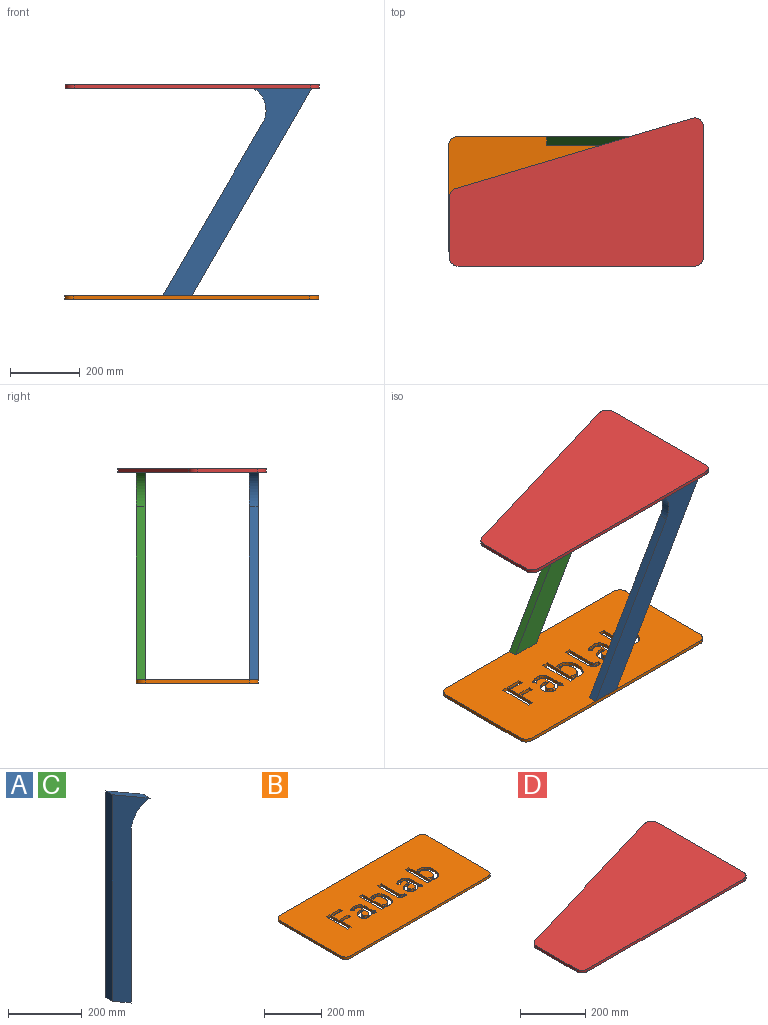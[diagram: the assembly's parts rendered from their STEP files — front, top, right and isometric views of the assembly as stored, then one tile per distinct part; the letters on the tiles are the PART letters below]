
ASSEMBLY  parts=4 mates=3
PART A: 7 faces, bbox 144x25x726 mm
  f0: plane 684.43x25mm, normal (-1,0,0), area 17110.8mm2, adj f3,f4,f5,f6
  f1: plane 570.86x25mm, normal (1,0,0), area 14271.5mm2, adj f2,f4,f5,f6
  f2: cylinder r=72mm len=72mm, axis (0,1,0), area 2827.4mm2, adj f1,f3,f4,f5
  f3: plane 144x83.14mm, normal (0.5,0,0.87), area 4156.9mm2, adj f0,f2,f4,f5
  f4: plane 726x144mm, normal (0,-1,0), area 51888mm2, adj f0,f1,f2,f3,f6
  f5: plane 726x144mm, normal (0,1,0), area 51888mm2, adj f0,f1,f2,f3,f6
  f6: plane 72x41.57mm, normal (-0.5,0,-0.87), area 2078.5mm2, adj f0,f1,f4,f5
PART B: 213 faces, bbox 726x348.5x10 mm
  f0: plane 298.48x10mm, normal (-1,0,0), area 2984.8mm2, adj f4,f5,f6,f9
  f1: plane 676x10mm, normal (0,-1,0), area 6760mm2, adj f4,f5,f6,f7
  f2: plane 298.48x10mm, normal (1,0,0), area 2984.8mm2, adj f4,f5,f7,f8
  f3: plane 676x10mm, normal (0,1,0), area 6760mm2, adj f4,f5,f8,f9
  f4: plane 726x348.48mm, normal (0,0,1), area 234382.8mm2, adj f0,f1,f2,f3,f6,f7,f8,f9
  f5: plane 726x348.48mm, normal (0,0,-1), area 234382.8mm2, adj f0,f1,f2,f3,f6,f7,f8,f9
  f6: cylinder r=25mm len=25mm, axis (0,0,1), area 392.7mm2, adj f0,f1,f4,f5
  f7: cylinder r=25mm len=25mm, axis (0,0,-1), area 392.7mm2, adj f1,f2,f4,f5
  f8: cylinder r=25mm len=25mm, axis (0,0,1), area 392.7mm2, adj f2,f3,f4,f5
  f9: cylinder r=25mm len=25mm, axis (0,0,-1), area 392.7mm2, adj f0,f3,f4,f5
  f10: plane 104.61x10mm, normal (1,0,0), area 1046.1mm2, adj f4,f5,f11,f212
  f11: plane 17.31x10mm, normal (0,-1,0), area 173.1mm2, adj f4,f5,f10,f12
  f12: plane 104.61x10mm, normal (-1,0,0), area 1046.1mm2, adj f4,f5,f11,f212
  f13: plane 11.65x10mm, normal (-1,0,0), area 116.5mm2, adj f4,f5,f14,f201
  f14: plane 37.88x10mm, normal (0,1,0), area 378.8mm2, adj f4,f5,f13,f15
  f15: plane 11.65x10mm, normal (1,0,0), area 116.5mm2, adj f4,f5,f14,f201
  f16: plane 42.29x10mm, normal (0,-1,0), area 422.9mm2, adj f4,f5,f17,f202
  f17: plane 12.9x10mm, normal (-1,0,0), area 129mm2, adj f4,f5,f16,f18
  f18: plane 42.29x10mm, normal (0,1,0), area 422.9mm2, adj f4,f5,f17,f202
  f19: extruded ~10x7.45mm, area 77.5mm2, adj f4,f5,f20,f203
  f20: extruded ~10x9.53mm, area 100.8mm2, adj f4,f5,f19,f21
  f21: extruded ~10x7.6mm, area 86.6mm2, adj f4,f5,f20,f22
  f22: plane 11.49x10mm, normal (-1,0,0), area 114.9mm2, adj f4,f5,f21,f23
  f23: extruded ~10x1.84mm, area 18.5mm2, adj f4,f5,f22,f24
  f24: extruded ~10x9.3mm, area 94.2mm2, adj f4,f5,f23,f25
  f25: extruded ~10x7.87mm, area 89.4mm2, adj f4,f5,f24,f26
  f26: extruded ~10x7.53mm, area 93.2mm2, adj f4,f5,f25,f27
  f27: extruded ~11.5x10mm, area 117.4mm2, adj f4,f5,f26,f28
  f28: extruded ~11.28x10mm, area 117.5mm2, adj f4,f5,f27,f29
  f29: extruded ~10x7.81mm, area 106.4mm2, adj f4,f5,f28,f30
  f30: extruded ~10x9.86mm, area 109.1mm2, adj f4,f5,f29,f31
  f31: extruded ~11.21x10mm, area 113.4mm2, adj f4,f5,f30,f32
  f32: plane 10x6.25mm, normal (0,-1,0), area 62.5mm2, adj f4,f5,f31,f33
  f33: plane 10.08x10mm, normal (-1,0,0), area 100.8mm2, adj f4,f5,f32,f34
  f34: plane 10x3.11mm, normal (0,1,0), area 31.1mm2, adj f4,f5,f33,f35
  f35: extruded ~10x5.96mm, area 60mm2, adj f4,f5,f34,f36
  f36: extruded ~10x5.83mm, area 62.3mm2, adj f4,f5,f35,f203
  f37: plane 19.58x10mm, normal (-1,0,0), area 195.8mm2, adj f4,f5,f38,f204
  f38: extruded ~10x3.34mm, area 33.4mm2, adj f4,f5,f37,f39
  f39: extruded ~10x4.47mm, area 45.1mm2, adj f4,f5,f38,f40
  f40: extruded ~10x4.11mm, area 43.4mm2, adj f4,f5,f39,f41
  f41: extruded ~10x2.49mm, area 35.5mm2, adj f4,f5,f40,f42
  f42: plane 10x9.52mm, normal (-0.9,0.43,0), area 105.4mm2, adj f4,f5,f41,f43
  f43: extruded ~10x3.91mm, area 40.2mm2, adj f4,f5,f42,f44
  f44: extruded ~10x3.97mm, area 46.6mm2, adj f4,f5,f43,f45
  f45: extruded ~10x3.48mm, area 47.8mm2, adj f4,f5,f44,f46
  f46: extruded ~10x4.19mm, area 46.9mm2, adj f4,f5,f45,f47
  f47: extruded ~10x6.31mm, area 85.8mm2, adj f4,f5,f46,f48
  f48: extruded ~10x9.3mm, area 101.9mm2, adj f4,f5,f47,f49
  f49: plane 10.79x10mm, normal (1,0,0), area 107.9mm2, adj f4,f5,f48,f50
  f50: extruded ~10x6.18mm, area 68.2mm2, adj f4,f5,f49,f51
  f51: extruded ~10x4.89mm, area 68.6mm2, adj f4,f5,f50,f52
  f52: plane 29.96x10mm, normal (1,0,0), area 299.6mm2, adj f4,f5,f51,f53
  f53: extruded ~11.07x10mm, area 111.1mm2, adj f4,f5,f52,f54
  f54: extruded ~10x6.04mm, area 65.9mm2, adj f4,f5,f53,f55
  f55: extruded ~10x4.19mm, area 49.2mm2, adj f4,f5,f54,f56
  f56: extruded ~10x5.89mm, area 59.2mm2, adj f4,f5,f55,f57
  f57: extruded ~10x5.88mm, area 59.5mm2, adj f4,f5,f56,f58
  f58: extruded ~10x5.11mm, area 54.4mm2, adj f4,f5,f57,f59
  f59: extruded ~10x4.11mm, area 47.4mm2, adj f4,f5,f58,f60
  f60: extruded ~10x2.63mm, area 33mm2, adj f4,f5,f59,f61
  f61: plane 10x9.79mm, normal (0.84,0.55,0), area 116.9mm2, adj f4,f5,f60,f62
  f62: extruded ~10x4.25mm, area 53.4mm2, adj f4,f5,f61,f63
  f63: extruded ~10x6.53mm, area 71.6mm2, adj f4,f5,f62,f64
  f64: extruded ~10x8.03mm, area 83mm2, adj f4,f5,f63,f65
  f65: extruded ~10x9.02mm, area 90.6mm2, adj f4,f5,f64,f66
  f66: extruded ~10x8.3mm, area 83.6mm2, adj f4,f5,f65,f67
  f67: extruded ~10x7.38mm, area 79.5mm2, adj f4,f5,f66,f68
  f68: extruded ~10x5.81mm, area 79.4mm2, adj f4,f5,f67,f69
  f69: extruded ~10x8.29mm, area 90.7mm2, adj f4,f5,f68,f70
  f70: extruded ~10.02x10mm, area 101.1mm2, adj f4,f5,f69,f204
  f71: plane 110.29x10mm, normal (1,0,0), area 1102.9mm2, adj f4,f5,f72,f205
  f72: plane 17.17x10mm, normal (0,-1,0), area 171.7mm2, adj f4,f5,f71,f73
  f73: plane 100.77x10mm, normal (-1,0,0), area 1007.7mm2, adj f4,f5,f72,f74
  f74: extruded ~10x4.55mm, area 45.7mm2, adj f4,f5,f73,f75
  f75: extruded ~10x4.96mm, area 49.8mm2, adj f4,f5,f74,f205
  f76: extruded ~11.64x10mm, area 128.7mm2, adj f4,f5,f77,f206
  f77: extruded ~14.33x10mm, area 144.7mm2, adj f4,f5,f76,f78
  f78: extruded ~15.75x10mm, area 159.1mm2, adj f4,f5,f77,f79
  f79: extruded ~13.56x10mm, area 148.3mm2, adj f4,f5,f78,f80
  f80: extruded ~10x9.79mm, area 136.7mm2, adj f4,f5,f79,f81
  f81: extruded ~13.83x10mm, area 144.4mm2, adj f4,f5,f80,f82
  f82: extruded ~10x9.52mm, area 96.1mm2, adj f4,f5,f81,f83
  f83: extruded ~10x7.81mm, area 84.4mm2, adj f4,f5,f82,f84
  f84: plane 14.76x10mm, normal (1,0,0), area 147.6mm2, adj f4,f5,f83,f85
  f85: extruded ~10x5.04mm, area 64.5mm2, adj f4,f5,f84,f86
  f86: extruded ~10x6.45mm, area 67mm2, adj f4,f5,f85,f87
  f87: extruded ~10x7.74mm, area 81.4mm2, adj f4,f5,f86,f88
  f88: extruded ~10x5.96mm, area 83.4mm2, adj f4,f5,f87,f89
  f89: extruded ~10x8.59mm, area 95mm2, adj f4,f5,f88,f90
  f90: extruded ~10.64x10mm, area 107.8mm2, adj f4,f5,f89,f91
  f91: extruded ~10.52x10mm, area 106.3mm2, adj f4,f5,f90,f92
  f92: extruded ~10x8.8mm, area 95.8mm2, adj f4,f5,f91,f93
  f93: extruded ~10x6.1mm, area 84.5mm2, adj f4,f5,f92,f94
  f94: extruded ~10x7.65mm, area 81mm2, adj f4,f5,f93,f95
  f95: extruded ~10x6.76mm, area 69.8mm2, adj f4,f5,f94,f96
  f96: extruded ~10x5.46mm, area 70.2mm2, adj f4,f5,f95,f97
  f97: plane 15.19x10mm, normal (1,0,0), area 151.9mm2, adj f4,f5,f96,f98
  f98: extruded ~10x7.25mm, area 78mm2, adj f4,f5,f97,f99
  f99: extruded ~10x8.22mm, area 83mm2, adj f4,f5,f98,f100
  f100: extruded ~10x9.53mm, area 96.4mm2, adj f4,f5,f99,f101
  f101: extruded ~10x9.01mm, area 100.2mm2, adj f4,f5,f100,f206
  f102: plane 85.87x10mm, normal (-1,0,0), area 858.7mm2, adj f4,f5,f103,f207
  f103: extruded ~10x7.59mm, area 77.5mm2, adj f4,f5,f102,f104
  f104: extruded ~10x4.12mm, area 55.2mm2, adj f4,f5,f103,f105
  f105: extruded ~10x5.18mm, area 55.1mm2, adj f4,f5,f104,f106
  f106: extruded ~10x6.31mm, area 63.3mm2, adj f4,f5,f105,f107
  f107: plane 10.52x10mm, normal (-1,0,0), area 105.2mm2, adj f4,f5,f106,f108
  f108: extruded ~10x3.82mm, area 38.4mm2, adj f4,f5,f107,f109
  f109: extruded ~10x3.7mm, area 37.1mm2, adj f4,f5,f108,f110
  f110: extruded ~10x4.25mm, area 42.5mm2, adj f4,f5,f109,f111
  f111: extruded ~10x4.27mm, area 42.7mm2, adj f4,f5,f110,f112
  f112: extruded ~10x3.84mm, area 38.6mm2, adj f4,f5,f111,f113
  f113: extruded ~10x7.52mm, area 88.1mm2, adj f4,f5,f112,f114
  f114: extruded ~10x7.3mm, area 84.3mm2, adj f4,f5,f113,f115
  f115: extruded ~10x7.88mm, area 81mm2, adj f4,f5,f114,f116
  f116: extruded ~10x5.97mm, area 59.9mm2, adj f4,f5,f115,f117
  f117: plane 85.01x10mm, normal (1,0,0), area 850.1mm2, adj f4,f5,f116,f207
  f118: extruded ~10x7.45mm, area 77.5mm2, adj f4,f5,f119,f208
  f119: extruded ~10x9.53mm, area 100.8mm2, adj f4,f5,f118,f120
  f120: extruded ~10x7.6mm, area 86.6mm2, adj f4,f5,f119,f121
  f121: plane 11.49x10mm, normal (-1,0,0), area 114.9mm2, adj f4,f5,f120,f122
  f122: extruded ~10x1.84mm, area 18.5mm2, adj f4,f5,f121,f123
  f123: extruded ~10x9.3mm, area 94.2mm2, adj f4,f5,f122,f124
  f124: extruded ~10x7.87mm, area 89.4mm2, adj f4,f5,f123,f125
  f125: extruded ~10x7.53mm, area 93.2mm2, adj f4,f5,f124,f126
  f126: extruded ~11.5x10mm, area 117.4mm2, adj f4,f5,f125,f127
  f127: extruded ~11.28x10mm, area 117.5mm2, adj f4,f5,f126,f128
  f128: extruded ~10x7.81mm, area 106.4mm2, adj f4,f5,f127,f129
  f129: extruded ~10x9.86mm, area 109.1mm2, adj f4,f5,f128,f130
  f130: extruded ~11.21x10mm, area 113.4mm2, adj f4,f5,f129,f131
  f131: plane 10x6.25mm, normal (0,-1,0), area 62.5mm2, adj f4,f5,f130,f132
  f132: plane 10.08x10mm, normal (-1,0,0), area 100.8mm2, adj f4,f5,f131,f133
  f133: plane 10x3.11mm, normal (0,1,0), area 31.1mm2, adj f4,f5,f132,f134
  f134: extruded ~10x5.96mm, area 60mm2, adj f4,f5,f133,f135
  f135: extruded ~10x5.83mm, area 62.3mm2, adj f4,f5,f134,f208
  f136: plane 19.58x10mm, normal (-1,0,0), area 195.8mm2, adj f4,f5,f137,f209
  f137: extruded ~10x3.34mm, area 33.4mm2, adj f4,f5,f136,f138
  f138: extruded ~10x4.47mm, area 45.1mm2, adj f4,f5,f137,f139
  f139: extruded ~10x4.11mm, area 43.4mm2, adj f4,f5,f138,f140
  f140: extruded ~10x2.49mm, area 35.5mm2, adj f4,f5,f139,f141
  f141: plane 10x9.52mm, normal (-0.9,0.43,0), area 105.4mm2, adj f4,f5,f140,f142
  f142: extruded ~10x3.91mm, area 40.2mm2, adj f4,f5,f141,f143
  f143: extruded ~10x3.97mm, area 46.6mm2, adj f4,f5,f142,f144
  f144: extruded ~10x3.48mm, area 47.8mm2, adj f4,f5,f143,f145
  f145: extruded ~10x4.19mm, area 46.9mm2, adj f4,f5,f144,f146
  f146: extruded ~10x6.31mm, area 85.8mm2, adj f4,f5,f145,f147
  f147: extruded ~10x9.3mm, area 101.9mm2, adj f4,f5,f146,f148
  f148: plane 10.79x10mm, normal (1,0,0), area 107.9mm2, adj f4,f5,f147,f149
  f149: extruded ~10x6.18mm, area 68.2mm2, adj f4,f5,f148,f150
  f150: extruded ~10x4.89mm, area 68.6mm2, adj f4,f5,f149,f151
  f151: plane 29.96x10mm, normal (1,0,0), area 299.6mm2, adj f4,f5,f150,f152
  f152: extruded ~11.07x10mm, area 111.1mm2, adj f4,f5,f151,f153
  f153: extruded ~10x6.04mm, area 65.9mm2, adj f4,f5,f152,f154
  f154: extruded ~10x4.19mm, area 49.2mm2, adj f4,f5,f153,f155
  f155: extruded ~10x5.89mm, area 59.2mm2, adj f4,f5,f154,f156
  f156: extruded ~10x5.88mm, area 59.5mm2, adj f4,f5,f155,f157
  f157: extruded ~10x5.11mm, area 54.4mm2, adj f4,f5,f156,f158
  f158: extruded ~10x4.11mm, area 47.4mm2, adj f4,f5,f157,f159
  f159: extruded ~10x2.63mm, area 33mm2, adj f4,f5,f158,f160
  f160: plane 10x9.79mm, normal (0.84,0.55,0), area 116.9mm2, adj f4,f5,f159,f161
  f161: extruded ~10x4.25mm, area 53.4mm2, adj f4,f5,f160,f162
  f162: extruded ~10x6.53mm, area 71.6mm2, adj f4,f5,f161,f163
  f163: extruded ~10x8.03mm, area 83mm2, adj f4,f5,f162,f164
  f164: extruded ~10x9.02mm, area 90.6mm2, adj f4,f5,f163,f165
  f165: extruded ~10x8.3mm, area 83.6mm2, adj f4,f5,f164,f166
  f166: extruded ~10x7.38mm, area 79.5mm2, adj f4,f5,f165,f167
  f167: extruded ~10x5.81mm, area 79.4mm2, adj f4,f5,f166,f168
  f168: extruded ~10x8.29mm, area 90.7mm2, adj f4,f5,f167,f169
  f169: extruded ~10.02x10mm, area 101.1mm2, adj f4,f5,f168,f209
  f170: plane 110.29x10mm, normal (1,0,0), area 1102.9mm2, adj f4,f5,f171,f210
  f171: plane 17.17x10mm, normal (0,-1,0), area 171.7mm2, adj f4,f5,f170,f172
  f172: plane 100.77x10mm, normal (-1,0,0), area 1007.7mm2, adj f4,f5,f171,f173
  f173: extruded ~10x4.55mm, area 45.7mm2, adj f4,f5,f172,f174
  f174: extruded ~10x4.96mm, area 49.8mm2, adj f4,f5,f173,f210
  f175: extruded ~11.64x10mm, area 128.7mm2, adj f4,f5,f176,f211
  f176: extruded ~14.33x10mm, area 144.7mm2, adj f4,f5,f175,f177
  f177: extruded ~15.75x10mm, area 159.1mm2, adj f4,f5,f176,f178
  f178: extruded ~13.56x10mm, area 148.3mm2, adj f4,f5,f177,f179
  f179: extruded ~10x9.79mm, area 136.7mm2, adj f4,f5,f178,f180
  f180: extruded ~13.83x10mm, area 144.4mm2, adj f4,f5,f179,f181
  f181: extruded ~10x9.52mm, area 96.1mm2, adj f4,f5,f180,f182
  f182: extruded ~10x7.81mm, area 84.4mm2, adj f4,f5,f181,f183
  f183: plane 14.76x10mm, normal (1,0,0), area 147.6mm2, adj f4,f5,f182,f184
  f184: extruded ~10x5.04mm, area 64.5mm2, adj f4,f5,f183,f185
  f185: extruded ~10x6.45mm, area 67mm2, adj f4,f5,f184,f186
  f186: extruded ~10x7.74mm, area 81.4mm2, adj f4,f5,f185,f187
  f187: extruded ~10x5.96mm, area 83.4mm2, adj f4,f5,f186,f188
  f188: extruded ~10x8.59mm, area 95mm2, adj f4,f5,f187,f189
  f189: extruded ~10.64x10mm, area 107.8mm2, adj f4,f5,f188,f190
  f190: extruded ~10.52x10mm, area 106.3mm2, adj f4,f5,f189,f191
  f191: extruded ~10x8.8mm, area 95.8mm2, adj f4,f5,f190,f192
  f192: extruded ~10x6.1mm, area 84.5mm2, adj f4,f5,f191,f193
  f193: extruded ~10x7.65mm, area 81mm2, adj f4,f5,f192,f194
  f194: extruded ~10x6.76mm, area 69.8mm2, adj f4,f5,f193,f195
  f195: extruded ~10x5.46mm, area 70.2mm2, adj f4,f5,f194,f196
  f196: plane 15.19x10mm, normal (1,0,0), area 151.9mm2, adj f4,f5,f195,f197
  f197: extruded ~10x7.25mm, area 78mm2, adj f4,f5,f196,f198
  f198: extruded ~10x8.22mm, area 83mm2, adj f4,f5,f197,f199
  f199: extruded ~10x9.53mm, area 96.4mm2, adj f4,f5,f198,f200
  f200: extruded ~10x9.01mm, area 100.2mm2, adj f4,f5,f199,f211
  f201: plane 37.88x10mm, normal (0,-1,0), area 378.8mm2, adj f4,f5,f13,f15
  f202: plane 12.9x10mm, normal (1,0,0), area 129mm2, adj f4,f5,f16,f18
  f203: extruded ~10x4.47mm, area 63.9mm2, adj f4,f5,f19,f36
  f204: extruded ~10.02x10mm, area 100.2mm2, adj f4,f5,f37,f70
  f205: plane 16.31x10mm, normal (0,1,0), area 163.1mm2, adj f4,f5,f71,f75
  f206: extruded ~10x7.81mm, area 109.9mm2, adj f4,f5,f76,f101
  f207: plane 17.33x10mm, normal (0,-1,0), area 173.3mm2, adj f4,f5,f102,f117
  f208: extruded ~10x4.47mm, area 63.9mm2, adj f4,f5,f118,f135
  f209: extruded ~10.02x10mm, area 100.2mm2, adj f4,f5,f136,f169
  f210: plane 16.31x10mm, normal (0,1,0), area 163.1mm2, adj f4,f5,f170,f174
  f211: extruded ~10x7.81mm, area 109.9mm2, adj f4,f5,f175,f200
  f212: plane 17.31x10mm, normal (0,1,0), area 173.1mm2, adj f4,f5,f10,f12
PART C: same geometry as A
PART D: 10 faces, bbox 726x423.5x10 mm
  f0: plane 172.36x10mm, normal (-1,0,0), area 1723.5mm2, adj f4,f5,f6,f9
  f1: plane 676x10mm, normal (0,-1,0), area 6760mm2, adj f4,f5,f6,f7
  f2: plane 373.48x10mm, normal (1,0,0), area 3734.8mm2, adj f4,f5,f7,f8
  f3: plane 676x201.12mm, normal (-0.29,0.96,0), area 7052.8mm2, adj f4,f5,f8,f9
  f4: plane 726x423.48mm, normal (0,0,1), area 234633.3mm2, adj f0,f1,f2,f3,f6,f7,f8,f9
  f5: plane 726x423.48mm, normal (0,0,-1), area 234633.3mm2, adj f0,f1,f2,f3,f6,f7,f8,f9
  f6: cylinder r=25mm len=25mm, axis (0,0,1), area 392.7mm2, adj f0,f1,f4,f5
  f7: cylinder r=25mm len=25mm, axis (0,0,-1), area 392.7mm2, adj f1,f2,f4,f5
  f8: cylinder r=25mm len=32.13mm, axis (0,0,1), area 465mm2, adj f2,f3,f4,f5
  f9: cylinder r=25mm len=23.96mm, axis (0,0,-1), area 320.4mm2, adj f0,f3,f4,f5
PLACE A rot(axis=(-0.26,0,-0.97),180deg) t=(-67.57,-145.4,-206.37)mm
PLACE B rot(axis=(0,-1,0),0deg) t=(-41.79,28.84,-602.73)mm
PLACE C rot(axis=(-0.26,0,-0.97),180deg) t=(-67.57,178.08,-206.37)mm
PLACE D t=(-40.15,48.1,0)mm
MATE fastened A.f3 <-> D.f5  axis (0,0,1) through (217.85,-132.9,0)mm
MATE fastened B.f4 <-> C.f6  axis (0,0,1) through (-41.79,203.08,-592.73)mm
MATE fastened C.f3 <-> D.f5  axis (0,0,1) through (217.85,190.58,0)mm
